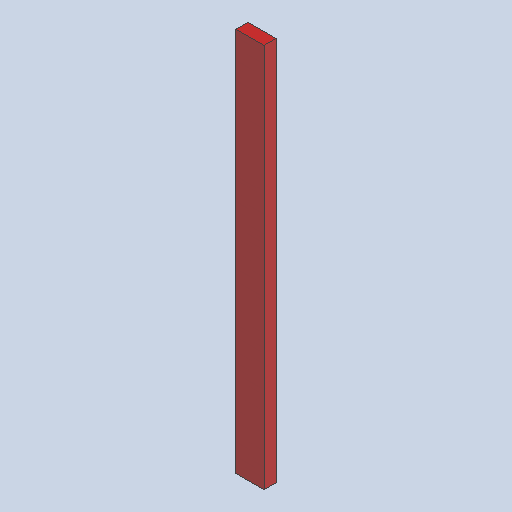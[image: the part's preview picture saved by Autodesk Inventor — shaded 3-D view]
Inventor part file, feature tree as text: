
AUTODESK INVENTOR PART (.ipt)
format: ipt  version: 2025 (Build 290162000, 162)  size: 87,552 bytes
history: native  units: in
note: dims shown in document units (in); Inventor stores cm internally (conversion verified against a paired STEP export)
features: extrude x1, sketch x1, other x1
ambient origin geometry x8: Origin, YZ Plane, XZ Plane, XY Plane, X Axis, Y Axis, Z Axis, Center Point
bodies: Solid1 (feature_tree)
feature tree (3):
  extrude  "Extrusion1"  Depth=3.5in
  sketch  "Sketch1"  dims[d0=1.5in d1=3.5in d2=48.0in d3=0.0in]
  other  "Finish1"
